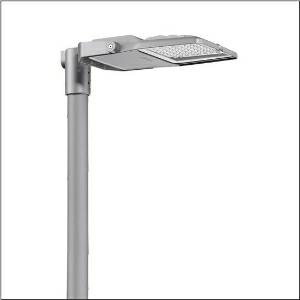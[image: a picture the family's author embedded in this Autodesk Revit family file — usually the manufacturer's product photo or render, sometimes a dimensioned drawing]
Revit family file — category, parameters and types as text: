
# Revit family: floodlight_fl_21_iq_mini___pl52_5xa7772b4d3a_2373
name_source: partatom
category: Lighting Fixtures
units: mm (PartAtom-declared; Revit-internal decimal feet)

## family parameters
Cut with Voids When Loaded = No
Host = Face
Light Source = No
Part Type = Normal
Room Calculation Point = No
Round Connector Dimension = Use Diameter
Shared = No

## types (1)
- --- (1 x LED, 6490 lm, 45.5 W, 4000K)
    Apparent Load = 46 VA
    CIE Flux Codes = 26 60 98 100 100
    Color Rendering = 70
    Color Temperature = 4000K
    Default Elevation = 1800 mm
    Description = Floodlight FL 21 iQ mini, floodlight, primary light control with lens, of PMMA, primary optical cover: protective disc, of toughened safety glass, transparent, light distribution: PL52, light emission: direct distribution, installation type: surface-mounted, lamps: LED, High Power LED, rated values: 6.490lm | 45,5W | 142,6lm/W (begin service life); end service life: 6.490lm | 48W; at 50% lumin. flux: 3.245lm | 21,5W | 150,9lm/W, colour temperature: 4000K, colour rendering: CRI > 70, light colour: 740, light setting 1 begin service life: 100% | 6.490lm | 45,5W | 142,6lm/W | 4.000K, light setting 1 end service life: 48W, further light settings possible, control: Street-Remote, Auto-Match, Temp-Guard, Night-Set, Smart-Wire, Desk-Remote (wireless, voltage-free reading and setting of iQ features in the workshop via application-optimized NFC function/RFID function), optimised constant luminous flux control (CLO 2.0), pre-setting: linear dimming characteristic, with terminal, 6-pole, mains connection: 220..240V, AC, 50/60Hz, luminaire housing, of diecast aluminium, powder-coated, SITECO metallic grey (DB 702S), corrosivity category C5 mid according to DIN EN ISO 12944suitable for swimming poolschlorine-resistant, sealing non-destructively replaceable, please order mast flange separately, mast bracket, of steel, galvanised, powder-coated, protection rating (complete): IP66, insulation class (complete): insulation class II (safety insulation), certification: CE, ENEC, VDE, protection symbol: D, impact resistance: IK08, permissible operating ambient temperature: -40..+40°C, permissible operating ambient temperature for outdoor applications: -40..+50°C, standard: DIN EN 12944, LABS conformity tested according to VDMA 24364:2018-05, packaging unit: 1 piece

Light Distribution: PL52
    Height = 70 mm
    Lamp = 1 x LED
    Lamp Light Flux = 6490 lm
    Lamp Power = 45.5 W
    Lamp count = 1
    Length = 485 mm
    Luminous efficacy = 143 lm/W
    Manufacturer = Siteco
    ModVariant = No
    Model = 5XA7772B4D3A
    Number of Poles = 1
    OnlyDefault = Yes
    Power Factor = 1
    Product Name = Floodlight FL 21 iQ mini | PL52
    Product group = floodlight | pylon annexe
    ProductGroupID = 6201
    Protection Class = Protection class II
    Protection Degree = IP 66
    RLX_Detail_Level = 1
    RLX_Emergency_Light_Flux = 0 lm
    RLX_Emergency_Type = 0
    RLX_Emergency_Type_DB = No
    RlxData = <blob elided: 101693 chars, md5=399a5c58>
    Socket = socket
    Standby Power = 0 W
    System Light Flux = 6490 lm
    System Power = 46 W
    Type Comments = factory setting: luminous flux: 100 % | dim-lin: 254 | 463 mA
    Type Image = l_1007125.jpg
    URL = http://relux.com
    VarID = @adj_164169
    Voltage = 0 V
    Weight = 0.00 kg
    Width = 337 mm

## geometry (parser evidence)
native form markers: Blend x4, Sweep x12
no freeform markers — native parametric forms only
